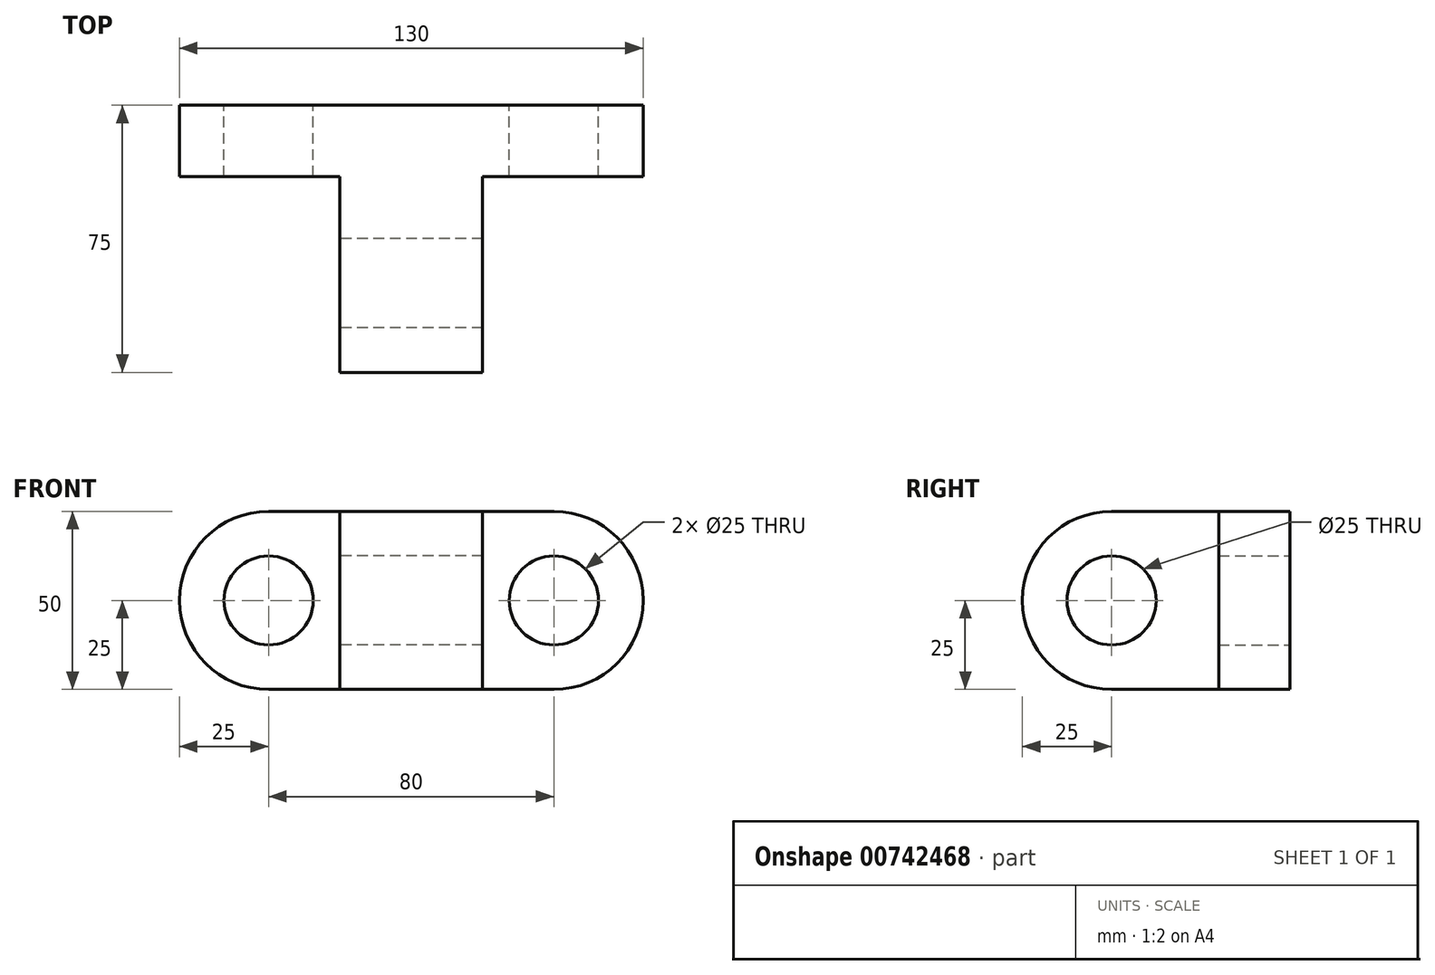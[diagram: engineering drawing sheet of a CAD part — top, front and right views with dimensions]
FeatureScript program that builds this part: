
annotation { "Feature Type Name" : "Feature", "Feature Type Description" : "" }
export const myFeature = defineFeature(function(context is Context, id is Id, definition is map)
    precondition{}
    {
        {
            var Q0;
            Q0=qCreatedBy(makeId("Front.planeOp"),FACE);
            var sketch = newSketch(context, id + "F0", { "sketchPlane" : qUnion([Q0])});
            skLineSegment(sketch, "E0.bottom", {"start": v(0, 0) * mm, "end": v(80, 0) * mm});
            skLineSegment(sketch, "E0.top", {"start": v(0, 50) * mm, "end": v(80, 50) * mm});
            skLineSegment(sketch, "E0.left", {"start": v(0, 0) * mm, "end": v(0, 50) * mm});
            skLineSegment(sketch, "E0.right", {"start": v(80, 0) * mm, "end": v(80, 50) * mm});
            skArc(sketch, "E1", {"start": v(0, 50) * mm, "mid": v(-25, 25) * mm, "end": v(0, 0) * mm});
            skArc(sketch, "E2", {"start": v(80, 0) * mm, "mid": v(105, 25) * mm, "end": v(80, 50) * mm});
            skCircle(sketch, "E3", {"center": v(0, 25) * mm, "radius": 12.5 * mm});
            skCircle(sketch, "E4", {"center": v(80, 25) * mm, "radius": 12.5 * mm});
            skLineSegment(sketch, "E5", {"start": v(20, 50) * mm, "end": v(20, 0) * mm});
            skLineSegment(sketch, "E6", {"start": v(60, 50) * mm, "end": v(60, 0) * mm});
            skSolve(sketch);
        }
        {
            var Q0;
            Q0 = qSketchRegion(id + "F0", true);
            extrude(context, id + "F1", {"entities" : qUnion([Q0]), "depth" : 20 * mm, "offsetDistance" : 25 * mm});
        }
        {
            var Q0;
            Q0=makeQuery(id+"F1.opExtrude","CAP_FACE",FACE,{"disambiguationData":[OSD([sQuery(id+"F0.wireOp",EDGE,"E0.bottom"),sQuery(id+"F0.wireOp",EDGE,"E0.top"),sQuery(id+"F0.wireOp",EDGE,"E1"),sQuery(id+"F0.wireOp",EDGE,"E2"),sQuery(id+"F0.wireOp",EDGE,"E3"),sQuery(id+"F0.wireOp",EDGE,"E4")])],"isStart":false});
            var sketch = newSketch(context, id + "F2", { "sketchPlane" : qUnion([Q0])});
            skLineSegment(sketch, "E7", {"start": v(40, 50) * mm, "end": v(40, 0) * mm, "construction": true});
            skLineSegment(sketch, "E8", {"start": v(20, 50) * mm, "end": v(20, 0) * mm});
            skLineSegment(sketch, "E9", {"start": v(60, 50) * mm, "end": v(60, 0) * mm});
            skSolve(sketch);
        }
        {
            var Q0;
            Q0 = qSketchRegion(id + "F2", true);
            var Q1;
            {var subQ0=sQuery(id+"F2.wireOp",EDGE,"E8");Q1=makeQuery(id+"F2.imprint","IMPRINT",FACE,{"disambiguationData":[TD([[makeQuery(id+"F2.imprint","IMPRINT",EDGE,{"derivedFrom":subQ0}),1.0]])]});}
            extrude(context, id + "F3", {"entities" : qUnion([Q0, Q1]), "operationType" : NewBodyOperationType.ADD, "depth" : 30 * mm, "offsetDistance" : 25 * mm});
        }
        {
            var Q0;
            Q0=makeQuery(id+"F3.opExtrude","SWEPT_FACE",FACE,{"disambiguationData":[OSD([sQuery(id+"F2.wireOp",EDGE,"E8")])]});
            var sketch = newSketch(context, id + "F4", { "sketchPlane" : qUnion([Q0])});
            skArc(sketch, "E10", {"start": v(50, 0) * mm, "mid": v(75, 25) * mm, "end": v(50, 50) * mm});
            skCircle(sketch, "E11", {"center": v(50, 25) * mm, "radius": 12.5 * mm});
            skSolve(sketch);
        }
        {
            var Q0;
            Q0 = qSketchRegion(id + "F4", true);
            var Q1;
            {var subQ0=sQuery(id+"F4.wireOp",EDGE,"E10");Q1=makeQuery(id+"F4.imprint","IMPRINT",FACE,{"disambiguationData":[TD([[makeQuery(id+"F4.imprint","IMPRINT",EDGE,{"derivedFrom":subQ0}),1.0]])]});}
            extrude(context, id + "F5", {"entities" : qUnion([Q0, Q1]), "operationType" : NewBodyOperationType.ADD, "oppositeDirection" : true, "depth" : 40 * mm, "offsetDistance" : 25 * mm});
        }
        {
            var Q0;
            Q0 = qSketchRegion(id + "F4", true);
            extrude(context, id + "F6", {"entities" : qUnion([Q0]), "operationType" : NewBodyOperationType.REMOVE, "endBound" : BoundingType.THROUGH_ALL, "oppositeDirection" : true, "depth" : 25 * mm, "offsetDistance" : 25 * mm});
        }
    });
